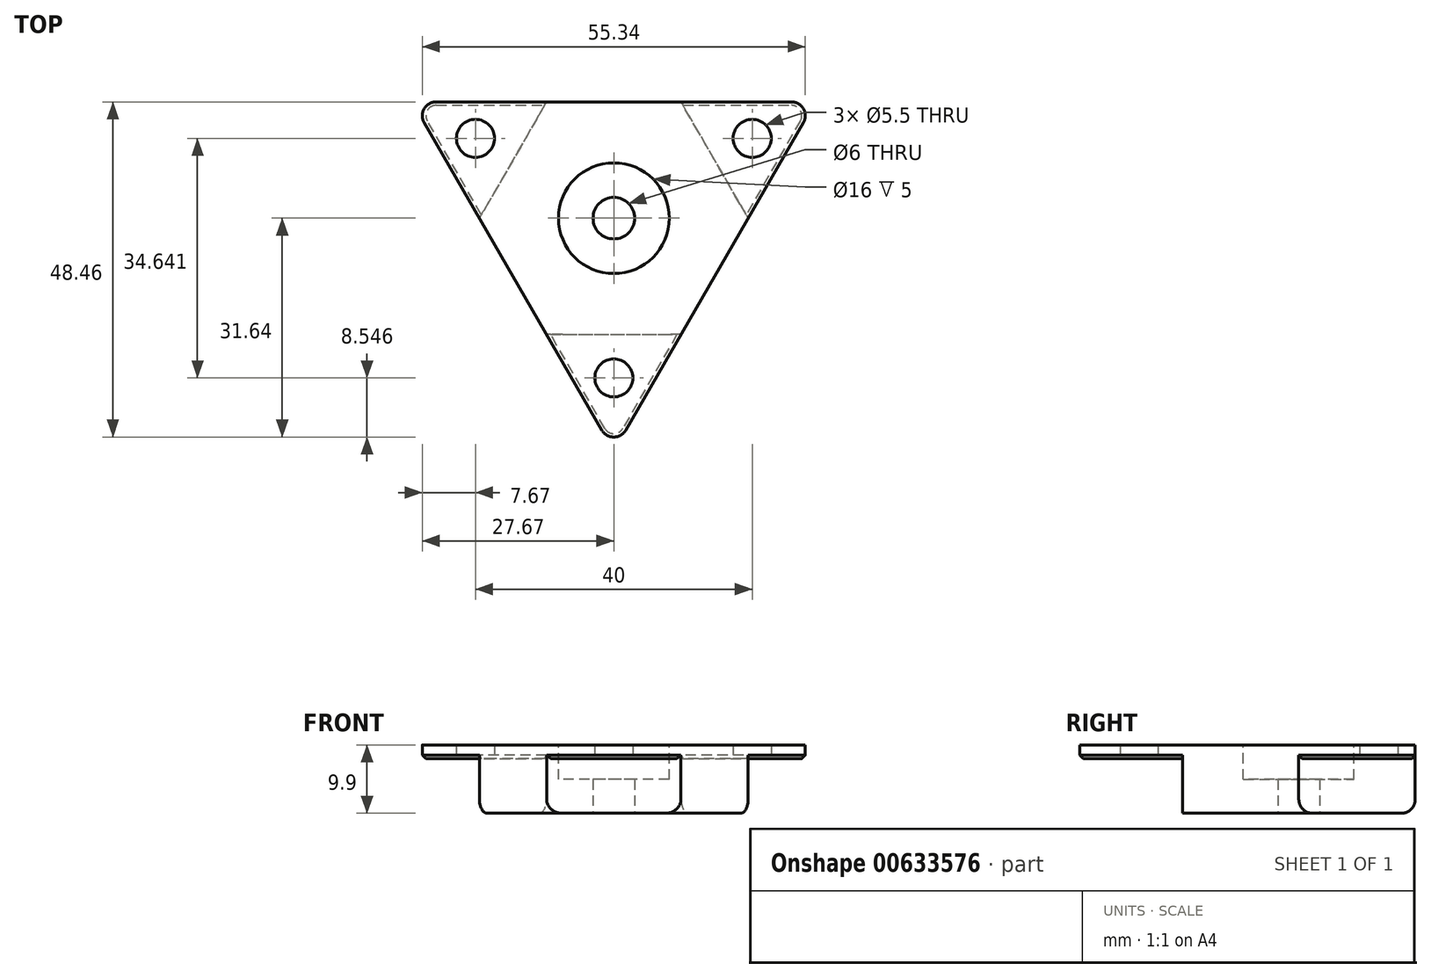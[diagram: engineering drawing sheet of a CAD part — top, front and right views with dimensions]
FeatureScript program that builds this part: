
annotation { "Feature Type Name" : "Feature", "Feature Type Description" : "" }
export const myFeature = defineFeature(function(context is Context, id is Id, definition is map)
    precondition{}
    {
        {
            var Q0;
            Q0=qCreatedBy(makeId("Top.planeOp"),FACE);
            var sketch = newSketch(context, id + "F0", { "sketchPlane" : qUnion([Q0])});
            skLineSegment(sketch, "E0", {"start": v(-30, 17.32) * mm, "end": v(30, 17.32) * mm, "construction": true});
            skLineSegment(sketch, "E1", {"start": v(30, 17.32) * mm, "end": v(0, -34.64) * mm, "construction": true});
            skLineSegment(sketch, "E2", {"start": v(0, -34.64) * mm, "end": v(-30, 17.32) * mm, "construction": true});
            skCircle(sketch, "E3", {"center": v(0, 0) * mm, "radius": 34.64 * mm, "construction": true});
            skCircle(sketch, "E4", {"center": v(-20, 11.55) * mm, "radius": 2.75 * mm});
            skLineSegment(sketch, "E5", {"start": v(-10, 17.32) * mm, "end": v(-20, 0) * mm, "construction": true});
            skLineSegment(sketch, "E6", {"start": v(-15, 8.66) * mm, "end": v(0, 0) * mm, "construction": true});
            skPoint(sketch, "E7.center", {"position": v(-45.27, -13.55) * mm});
            skCircle(sketch, "E8", {"center": v(-20, 11.55) * mm, "radius": 5.77 * mm, "construction": true});
            skCircle(sketch, "E9", {"center": v(0, 0) * mm, "radius": 10 * mm, "construction": true});
            skCircle(sketch, "E10", {"center": v(0, 0) * mm, "radius": 3 * mm});
            skLineSegment(sketch, "E11.0", {"start": v(0, -33.64) * mm, "end": v(-29.13, 16.82) * mm});
            skLineSegment(sketch, "E11.1", {"start": v(29.13, 16.82) * mm, "end": v(0, -33.64) * mm});
            skLineSegment(sketch, "E11.2", {"start": v(-29.13, 16.82) * mm, "end": v(29.13, 16.82) * mm});
            skLineSegment(sketch, "E12.0", {"start": v(-9.71, 16.82) * mm, "end": v(-19.42, 0) * mm});
            skCircle(sketch, "E13.1.0", {"center": v(0, -23.1) * mm, "radius": 2.75 * mm});
            skLineSegment(sketch, "E13.1.1", {"start": v(-9.71, -16.82) * mm, "end": v(9.71, -16.82) * mm});
            skCircle(sketch, "E13.2.0", {"center": v(20, 11.55) * mm, "radius": 2.75 * mm});
            skLineSegment(sketch, "E13.2.1", {"start": v(19.42, 0) * mm, "end": v(9.71, 16.82) * mm});
            skSolve(sketch);
        }
        {
            var Q0;
            Q0=qSketchRegion(id+"F0",true);
            extrude(context, id + "F1", {"entities" : qUnion([Q0]), "depth" : 9.9 * mm});
        }
        {
            var Q0;
            Q0=makeQuery(id+"F0.imprint","IMPRINT",FACE,{"disambiguationData":[TD([[makeQuery(id+"F0.imprint","IMPRINT",EDGE,{"derivedFrom":sQuery(id+"F0.wireOp",EDGE,"E13.2.0")}),-1.0]])]});
            var Q1;
            Q1=makeQuery(id+"F0.imprint","IMPRINT",FACE,{"disambiguationData":[TD([[makeQuery(id+"F0.imprint","IMPRINT",EDGE,{"derivedFrom":sQuery(id+"F0.wireOp",EDGE,"E13.1.0")}),-1.0]])]});
            var Q2;
            Q2=makeQuery(id+"F0.imprint","IMPRINT",FACE,{"disambiguationData":[TD([[makeQuery(id+"F0.imprint","IMPRINT",EDGE,{"derivedFrom":sQuery(id+"F0.wireOp",EDGE,"E4")}),-1.0]])]});
            extrude(context, id + "F2", {"entities" : qUnion([Q0, Q1, Q2]), "operationType" : NewBodyOperationType.REMOVE, "depth" : 7.9 * mm});
        }
        {
            var Q0;
            Q0=makeQuery(id+"F1.opExtrude","CAP_FACE",FACE,{"disambiguationData":[OSD([sQuery(id+"F0.wireOp",EDGE,"E0"),sQuery(id+"F0.wireOp",EDGE,"E1"),sQuery(id+"F0.wireOp",EDGE,"E2"),sQuery(id+"F0.wireOp",EDGE,"E4"),sQuery(id+"F0.wireOp",EDGE,"3f91073c-f4cf-4afd-b99c-0fb4fe4cd3df.1.0"),sQuery(id+"F0.wireOp",EDGE,"3f91073c-f4cf-4afd-b99c-0fb4fe4cd3df.2.0"),sQuery(id+"F0.wireOp",EDGE,"E10")])],"isStart":false});
            var sketch = newSketch(context, id + "F3", { "sketchPlane" : qUnion([Q0])});
            skCircle(sketch, "E14", {"center": v(0, 0) * mm, "radius": 8 * mm});
            skSolve(sketch);
        }
        {
            var Q0;
            Q0=makeQuery(id+"F3.imprint","IMPRINT",FACE,{"disambiguationData":[TD([[makeQuery(id+"F3.imprint","IMPRINT",EDGE,{"derivedFrom":sQuery(id+"F3.wireOp",EDGE,"E14")}),1.0]])]});
            extrude(context, id + "F4", {"entities" : qUnion([Q0]), "operationType" : NewBodyOperationType.REMOVE, "oppositeDirection" : true, "depth" : 5 * mm});
        }
        {
            var Q0;
            Q0=makeQuery(id+"F1.opExtrude","SWEPT_EDGE",EDGE,{"disambiguationData":[OSD([sQuery(id+"F0.wireOp",EDGE,"E11.0"),sQuery(id+"F0.wireOp",EDGE,"E11.2")])]});
            var Q1;
            Q1=makeQuery(id+"F2.boolean.opBoolean","COPY",EDGE,{"derivedFrom":makeQuery(id+"F2.opExtrude","SWEPT_EDGE",EDGE,{"disambiguationData":[OSD([sQuery(id+"F0.wireOp",EDGE,"E11.2"),sQuery(id+"F0.wireOp",EDGE,"E12.0")])]})});
            var Q2;
            Q2=makeQuery(id+"F2.boolean.opBoolean","COPY",EDGE,{"derivedFrom":makeQuery(id+"F2.opExtrude","SWEPT_EDGE",EDGE,{"disambiguationData":[OSD([sQuery(id+"F0.wireOp",EDGE,"E11.0"),sQuery(id+"F0.wireOp",EDGE,"E12.0")])]})});
            var Q3;
            Q3=makeQuery(id+"F2.boolean.opBoolean","COPY",EDGE,{"derivedFrom":makeQuery(id+"F2.opExtrude","SWEPT_EDGE",EDGE,{"disambiguationData":[OSD([sQuery(id+"F0.wireOp",EDGE,"E11.2"),sQuery(id+"F0.wireOp",EDGE,"E13.2.1")])]})});
            var Q4;
            Q4=makeQuery(id+"F2.boolean.opBoolean","COPY",EDGE,{"derivedFrom":makeQuery(id+"F2.opExtrude","CAP_EDGE",EDGE,{"disambiguationData":[OSD([sQuery(id+"F0.wireOp",EDGE,"E13.2.1")])],"isStart":true})});
            var Q5;
            Q5=makeQuery(id+"F1.opExtrude","CAP_EDGE",EDGE,{"disambiguationData":[OSD([sQuery(id+"F0.wireOp",EDGE,"E11.2")])],"isStart":true});
            var Q6;
            Q6=makeQuery(id+"F2.boolean.opBoolean","COPY",EDGE,{"derivedFrom":makeQuery(id+"F2.opExtrude","CAP_EDGE",EDGE,{"disambiguationData":[OSD([sQuery(id+"F0.wireOp",EDGE,"E12.0")])],"isStart":true})});
            var Q7;
            Q7=makeQuery(id+"F1.opExtrude","CAP_EDGE",EDGE,{"disambiguationData":[OSD([sQuery(id+"F0.wireOp",EDGE,"E11.0")])],"isStart":true});
            var Q8;
            Q8=makeQuery(id+"F2.boolean.opBoolean","COPY",EDGE,{"derivedFrom":makeQuery(id+"F2.opExtrude","CAP_EDGE",EDGE,{"disambiguationData":[OSD([sQuery(id+"F0.wireOp",EDGE,"E13.1.1")])],"isStart":true})});
            var Q9;
            Q9=makeQuery(id+"F2.boolean.opBoolean","COPY",EDGE,{"derivedFrom":makeQuery(id+"F2.opExtrude","SWEPT_EDGE",EDGE,{"disambiguationData":[OSD([sQuery(id+"F0.wireOp",EDGE,"E11.1"),sQuery(id+"F0.wireOp",EDGE,"E13.2.1")])]})});
            var Q10;
            Q10=makeQuery(id+"F2.boolean.opBoolean","COPY",EDGE,{"derivedFrom":makeQuery(id+"F2.opExtrude","SWEPT_EDGE",EDGE,{"disambiguationData":[OSD([sQuery(id+"F0.wireOp",EDGE,"E11.1"),sQuery(id+"F0.wireOp",EDGE,"E13.1.1")])]})});
            var Q11;
            Q11=makeQuery(id+"F1.opExtrude","SWEPT_EDGE",EDGE,{"disambiguationData":[OSD([sQuery(id+"F0.wireOp",EDGE,"E11.0"),sQuery(id+"F0.wireOp",EDGE,"E11.1")])]});
            var Q12;
            Q12=makeQuery(id+"F1.opExtrude","SWEPT_EDGE",EDGE,{"disambiguationData":[OSD([sQuery(id+"F0.wireOp",EDGE,"E11.1"),sQuery(id+"F0.wireOp",EDGE,"E11.2")])]});
            var Q13;
            Q13=makeQuery(id+"F2.boolean.opBoolean","COPY",EDGE,{"derivedFrom":makeQuery(id+"F2.opExtrude","SWEPT_EDGE",EDGE,{"disambiguationData":[OSD([sQuery(id+"F0.wireOp",EDGE,"E11.0"),sQuery(id+"F0.wireOp",EDGE,"E13.1.1")])]})});
            var Q14;
            Q14=makeQuery(id+"F1.opExtrude","CAP_EDGE",EDGE,{"disambiguationData":[OSD([sQuery(id+"F0.wireOp",EDGE,"E11.1")])],"isStart":true});
            fillet(context, id + "F5", {"entities" : qUnion([Q0, Q1, Q2, Q3, Q4, Q5, Q6, Q7, Q8, Q9, Q10, Q11, Q12, Q13, Q14]), "radius" : 2 * mm, "tangentPropagation" : true, "allowEdgeOverflow" : false});
        }
        {
            var Q0;
            {var subQ0=sQuery(id+"F0.wireOp",EDGE,"E11.1");var subQ1=sQuery(id+"F0.wireOp",EDGE,"E11.0");Q0=makeQuery(id+"F5.opFillet","BLEND_EDGE",EDGE,{"blendedFrom":[makeQuery(id+"F1.opExtrude","SWEPT_EDGE",EDGE,{"disambiguationData":[OSD([subQ1,subQ0])]}),makeQuery(id+"F2.boolean.opBoolean","COPY",FACE,{"derivedFrom":makeQuery(id+"F2.opExtrude","CAP_FACE",FACE,{"disambiguationData":[OSD([subQ1,subQ0,sQuery(id+"F0.wireOp",EDGE,"E13.1.0"),sQuery(id+"F0.wireOp",EDGE,"E13.1.1")])],"isStart":false})})],"blendedInto":[makeQuery(id+"F2.boolean.opBoolean","COPY",FACE,{"derivedFrom":makeQuery(id+"F2.opExtrude","CAP_FACE",FACE,{"disambiguationData":[OSD([subQ1,subQ0,sQuery(id+"F0.wireOp",EDGE,"E13.1.0"),sQuery(id+"F0.wireOp",EDGE,"E13.1.1")])],"isStart":false})})]});}
            var Q1;
            {var subQ0=sQuery(id+"F0.wireOp",EDGE,"E11.2");var subQ1=sQuery(id+"F0.wireOp",EDGE,"E11.0");Q1=makeQuery(id+"F5.opFillet","BLEND_EDGE",EDGE,{"blendedFrom":[makeQuery(id+"F1.opExtrude","SWEPT_EDGE",EDGE,{"disambiguationData":[OSD([subQ1,subQ0])]}),makeQuery(id+"F2.boolean.opBoolean","COPY",FACE,{"derivedFrom":makeQuery(id+"F2.opExtrude","CAP_FACE",FACE,{"disambiguationData":[OSD([sQuery(id+"F0.wireOp",EDGE,"E4"),subQ1,subQ0,sQuery(id+"F0.wireOp",EDGE,"E12.0")])],"isStart":false})})],"blendedInto":[makeQuery(id+"F2.boolean.opBoolean","COPY",FACE,{"derivedFrom":makeQuery(id+"F2.opExtrude","CAP_FACE",FACE,{"disambiguationData":[OSD([sQuery(id+"F0.wireOp",EDGE,"E4"),subQ1,subQ0,sQuery(id+"F0.wireOp",EDGE,"E12.0")])],"isStart":false})})]});}
            var Q2;
            {var subQ0=sQuery(id+"F0.wireOp",EDGE,"E11.2");var subQ1=sQuery(id+"F0.wireOp",EDGE,"E11.1");Q2=makeQuery(id+"F5.opFillet","BLEND_EDGE",EDGE,{"blendedFrom":[makeQuery(id+"F1.opExtrude","SWEPT_EDGE",EDGE,{"disambiguationData":[OSD([subQ1,subQ0])]}),makeQuery(id+"F2.boolean.opBoolean","COPY",FACE,{"derivedFrom":makeQuery(id+"F2.opExtrude","CAP_FACE",FACE,{"disambiguationData":[OSD([subQ1,subQ0,sQuery(id+"F0.wireOp",EDGE,"E13.2.0"),sQuery(id+"F0.wireOp",EDGE,"E13.2.1")])],"isStart":false})})],"blendedInto":[makeQuery(id+"F2.boolean.opBoolean","COPY",FACE,{"derivedFrom":makeQuery(id+"F2.opExtrude","CAP_FACE",FACE,{"disambiguationData":[OSD([subQ1,subQ0,sQuery(id+"F0.wireOp",EDGE,"E13.2.0"),sQuery(id+"F0.wireOp",EDGE,"E13.2.1")])],"isStart":false})})]});}
            chamfer(context, id + "F6", {"entities" : qUnion([Q0, Q1, Q2]), "width" : 0.5 * mm, "tangentPropagation" : true});
        }
    });
